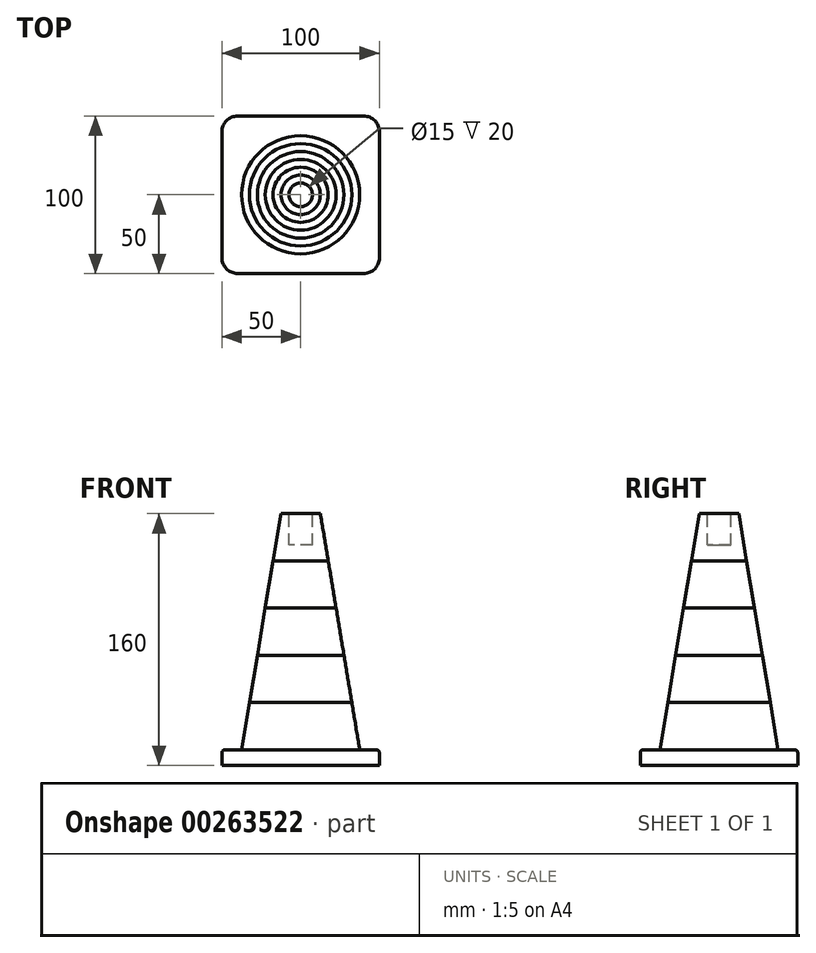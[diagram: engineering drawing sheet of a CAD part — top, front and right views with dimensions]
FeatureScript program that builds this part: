
annotation { "Feature Type Name" : "Feature", "Feature Type Description" : "" }
export const myFeature = defineFeature(function(context is Context, id is Id, definition is map)
    precondition{}
    {
        {
            var Q0;
            Q0=qCreatedBy(makeId("Top.planeOp"),FACE);
            var sketch = newSketch(context, id + "F0", { "sketchPlane" : qUnion([Q0])});
            skLineSegment(sketch, "E0.bottom", {"start": v(-40, 50) * mm, "end": v(40, 50) * mm});
            skLineSegment(sketch, "E0.top", {"start": v(-40, -50) * mm, "end": v(40, -50) * mm});
            skLineSegment(sketch, "E0.left", {"start": v(-50, 40) * mm, "end": v(-50, -40) * mm});
            skLineSegment(sketch, "E0.right", {"start": v(50, 40) * mm, "end": v(50, -40) * mm});
            skPoint(sketch, "E1.visualSharp", {"position": v(-50, 50) * mm});
            skArc(sketch, "E1.filletArc", {"start": v(-40, 50) * mm, "mid": v(-47.07, 47.07) * mm, "end": v(-50, 40) * mm});
            skPoint(sketch, "E2.visualSharp", {"position": v(50, 50) * mm});
            skArc(sketch, "E2.filletArc", {"start": v(50, 40) * mm, "mid": v(47.07, 47.07) * mm, "end": v(40, 50) * mm});
            skPoint(sketch, "E3.visualSharp", {"position": v(50, -50) * mm});
            skArc(sketch, "E3.filletArc", {"start": v(40, -50) * mm, "mid": v(47.07, -47.07) * mm, "end": v(50, -40) * mm});
            skPoint(sketch, "E4.visualSharp", {"position": v(-50, -50) * mm});
            skArc(sketch, "E4.filletArc", {"start": v(-50, -40) * mm, "mid": v(-47.07, -47.07) * mm, "end": v(-40, -50) * mm});
            skSolve(sketch);
        }
        {
            var Q0;
            Q0=makeQuery(id+"F0.imprint","IMPRINT",FACE,{"disambiguationData":[TD([[makeQuery(id+"F0.imprint","IMPRINT",EDGE,{"derivedFrom":sQuery(id+"F0.wireOp",EDGE,"E0.bottom")}),-1.0]])]});
            extrude(context, id + "F1", {"entities" : qUnion([Q0]), "depth" : 10 * mm});
        }
        {
            var Q0;
            Q0=makeQuery(id+"F1.opExtrude","CAP_FACE",FACE,{"disambiguationData":[OSD([sQuery(id+"F0.wireOp",EDGE,"E0.bottom"),sQuery(id+"F0.wireOp",EDGE,"E0.top"),sQuery(id+"F0.wireOp",EDGE,"E0.left"),sQuery(id+"F0.wireOp",EDGE,"E0.right")])],"isStart":false});
            var sketch = newSketch(context, id + "F2", { "sketchPlane" : qUnion([Q0])});
            skLineSegment(sketch, "E5.0.0", {"start": v(-50, 40) * mm, "end": v(-50, -40) * mm});
            skLineSegment(sketch, "E5.0.1", {"start": v(-50, -50) * mm, "end": v(-40, -50) * mm});
            skLineSegment(sketch, "E5.0.2", {"start": v(50, -50) * mm, "end": v(50, 40) * mm});
            skLineSegment(sketch, "E5.0.3", {"start": v(50, 50) * mm, "end": v(-50, 50) * mm});
            skCircle(sketch, "E6", {"center": v(0, 0) * mm, "radius": 37.5 * mm});
            skSolve(sketch);
        }
        {
            var Q0;
            Q0=qCreatedBy(makeId("Top.planeOp"),FACE);
            cPlane(context, id + "F3", {"entities" : qUnion([Q0]), "cplaneType" : CPlaneType.OFFSET, "offset" : 40 * mm, "width" : 150 * mm, "height" : 150 * mm});
        }
        {
            var Q0;
            Q0=qCreatedBy(id+"F3.planeOp",FACE);
            var sketch = newSketch(context, id + "F4", { "sketchPlane" : qUnion([Q0])});
            skCircle(sketch, "E7.0", {"center": v(0, 0) * mm, "radius": 37.5 * mm});
            skCircle(sketch, "E8", {"center": v(0, 0) * mm, "radius": 32.5 * mm});
            skSolve(sketch);
        }
        {
            var Q1;
            Q1=makeQuery(id+"F2.imprint","IMPRINT",FACE,{"disambiguationData":[TD([[makeQuery(id+"F2.imprint","IMPRINT",EDGE,{"derivedFrom":sQuery(id+"F2.wireOp",EDGE,"E6")}),1.0]])]});
            var Q2;
            Q2=makeQuery(id+"F4.imprint","IMPRINT",FACE,{"disambiguationData":[TD([[makeQuery(id+"F4.imprint","IMPRINT",EDGE,{"derivedFrom":sQuery(id+"F4.wireOp",EDGE,"E8")}),1.0]])]});
            loft(context, id + "F5", {"sheetProfilesArray" : [{ "sheetProfileEntities" : qUnion([Q1]) }, { "sheetProfileEntities" : qUnion([Q2]) }]});
        }
        {
            var Q0;
            Q0=qCreatedBy(id+"F3.planeOp",FACE);
            cPlane(context, id + "F6", {"entities" : qUnion([Q0]), "cplaneType" : CPlaneType.OFFSET, "offset" : 30 * mm, "width" : 150 * mm, "height" : 150 * mm});
        }
        {
            var Q0;
            Q0=qCreatedBy(id+"F6.planeOp",FACE);
            var sketch = newSketch(context, id + "F7", { "sketchPlane" : qUnion([Q0])});
            skCircle(sketch, "E9.0.0", {"center": v(0, 0) * mm, "radius": 32.5 * mm});
            skCircle(sketch, "E10", {"center": v(0, 0) * mm, "radius": 27.5 * mm});
            skSolve(sketch);
        }
        {
            var Q1;
            Q1=makeQuery(id+"F5.opLoft","CAP_FACE",FACE,{"disambiguationData":[OSD([makeQuery(id+"F4.imprint","IMPRINT",FACE,{"disambiguationData":[TD([[makeQuery(id+"F4.imprint","IMPRINT",EDGE,{"derivedFrom":sQuery(id+"F4.wireOp",EDGE,"E8")}),1.0]])]})])],"isStart":true});
            var Q2;
            Q2=makeQuery(id+"F7.imprint","IMPRINT",FACE,{"disambiguationData":[TD([[makeQuery(id+"F7.imprint","IMPRINT",EDGE,{"derivedFrom":sQuery(id+"F7.wireOp",EDGE,"E10")}),1.0]])]});
            loft(context, id + "F8", {"sheetProfilesArray" : [{ "sheetProfileEntities" : qUnion([Q1]) }, { "sheetProfileEntities" : qUnion([Q2]) }]});
        }
        {
            var Q0;
            Q0=qCreatedBy(id+"F6.planeOp",FACE);
            cPlane(context, id + "F9", {"entities" : qUnion([Q0]), "cplaneType" : CPlaneType.OFFSET, "offset" : 30 * mm, "width" : 150 * mm, "height" : 150 * mm});
        }
        {
            var Q0;
            Q0=qCreatedBy(id+"F9.planeOp",FACE);
            var sketch = newSketch(context, id + "F10", { "sketchPlane" : qUnion([Q0])});
            skCircle(sketch, "E11.0.0", {"center": v(0, 0) * mm, "radius": 27.5 * mm});
            skCircle(sketch, "E12", {"center": v(0, 0) * mm, "radius": 22.5 * mm});
            skSolve(sketch);
        }
        {
            var Q1;
            Q1=makeQuery(id+"F8.opLoft","CAP_FACE",FACE,{"disambiguationData":[OSD([makeQuery(id+"F7.imprint","IMPRINT",FACE,{"disambiguationData":[TD([[makeQuery(id+"F7.imprint","IMPRINT",EDGE,{"derivedFrom":sQuery(id+"F7.wireOp",EDGE,"E10")}),1.0]])]})])],"isStart":true});
            var Q2;
            Q2=makeQuery(id+"F10.imprint","IMPRINT",FACE,{"disambiguationData":[TD([[makeQuery(id+"F10.imprint","IMPRINT",EDGE,{"derivedFrom":sQuery(id+"F10.wireOp",EDGE,"E12")}),1.0]])]});
            loft(context, id + "F11", {"sheetProfilesArray" : [{ "sheetProfileEntities" : qUnion([Q1]) }, { "sheetProfileEntities" : qUnion([Q2]) }]});
        }
        {
            var Q0;
            Q0=qCreatedBy(id+"F9.planeOp",FACE);
            cPlane(context, id + "F12", {"entities" : qUnion([Q0]), "cplaneType" : CPlaneType.OFFSET, "offset" : 30 * mm, "width" : 150 * mm, "height" : 150 * mm});
        }
        {
            var Q0;
            Q0=qCreatedBy(id+"F12.planeOp",FACE);
            var sketch = newSketch(context, id + "F13", { "sketchPlane" : qUnion([Q0])});
            skCircle(sketch, "E13.0.0", {"center": v(0, 0) * mm, "radius": 22.5 * mm});
            skCircle(sketch, "E14", {"center": v(0, 0) * mm, "radius": 17.5 * mm});
            skSolve(sketch);
        }
        {
            var Q1;
            Q1=makeQuery(id+"F11.opLoft","CAP_FACE",FACE,{"disambiguationData":[OSD([makeQuery(id+"F10.imprint","IMPRINT",FACE,{"disambiguationData":[TD([[makeQuery(id+"F10.imprint","IMPRINT",EDGE,{"derivedFrom":sQuery(id+"F10.wireOp",EDGE,"E12")}),1.0]])]})])],"isStart":true});
            var Q2;
            Q2=makeQuery(id+"F13.imprint","IMPRINT",FACE,{"disambiguationData":[TD([[makeQuery(id+"F13.imprint","IMPRINT",EDGE,{"derivedFrom":sQuery(id+"F13.wireOp",EDGE,"E14")}),1.0]])]});
            loft(context, id + "F14", {"sheetProfilesArray" : [{ "sheetProfileEntities" : qUnion([Q1]) }, { "sheetProfileEntities" : qUnion([Q2]) }]});
        }
        {
            var Q0;
            Q0=qCreatedBy(id+"F12.planeOp",FACE);
            cPlane(context, id + "F15", {"entities" : qUnion([Q0]), "cplaneType" : CPlaneType.OFFSET, "offset" : 30 * mm, "width" : 150 * mm, "height" : 150 * mm});
        }
        {
            var Q0;
            Q0=qCreatedBy(id+"F15.planeOp",FACE);
            var sketch = newSketch(context, id + "F16", { "sketchPlane" : qUnion([Q0])});
            skCircle(sketch, "E15.0.0", {"center": v(0, 0) * mm, "radius": 17.5 * mm});
            skCircle(sketch, "E16", {"center": v(0, 0) * mm, "radius": 12.5 * mm});
            skSolve(sketch);
        }
        {
            var Q1;
            Q1=makeQuery(id+"F14.opLoft","CAP_FACE",FACE,{"disambiguationData":[OSD([makeQuery(id+"F13.imprint","IMPRINT",FACE,{"disambiguationData":[TD([[makeQuery(id+"F13.imprint","IMPRINT",EDGE,{"derivedFrom":sQuery(id+"F13.wireOp",EDGE,"E14")}),1.0]])]})])],"isStart":true});
            var Q2;
            Q2=makeQuery(id+"F16.imprint","IMPRINT",FACE,{"disambiguationData":[TD([[makeQuery(id+"F16.imprint","IMPRINT",EDGE,{"derivedFrom":sQuery(id+"F16.wireOp",EDGE,"E16")}),1.0]])]});
            loft(context, id + "F17", {"sheetProfilesArray" : [{ "sheetProfileEntities" : qUnion([Q1]) }, { "sheetProfileEntities" : qUnion([Q2]) }]});
        }
        {
            var Q0;
            Q0=makeQuery(id+"F1.opExtrude","CAP_EDGE",EDGE,{"disambiguationData":[OSD([sQuery(id+"F0.wireOp",EDGE,"E0.top")])],"isStart":false});
            var Q1;
            Q1=makeQuery(id+"F1.opExtrude","CAP_EDGE",EDGE,{"disambiguationData":[OSD([sQuery(id+"F0.wireOp",EDGE,"E4.filletArc")])],"isStart":false});
            var Q2;
            Q2=makeQuery(id+"F1.opExtrude","CAP_EDGE",EDGE,{"disambiguationData":[OSD([sQuery(id+"F0.wireOp",EDGE,"E0.left")])],"isStart":false});
            var Q3;
            Q3=makeQuery(id+"F1.opExtrude","CAP_EDGE",EDGE,{"disambiguationData":[OSD([sQuery(id+"F0.wireOp",EDGE,"E3.filletArc")])],"isStart":false});
            var Q4;
            Q4=makeQuery(id+"F1.opExtrude","CAP_EDGE",EDGE,{"disambiguationData":[OSD([sQuery(id+"F0.wireOp",EDGE,"E0.right")])],"isStart":false});
            var Q5;
            Q5=makeQuery(id+"F1.opExtrude","CAP_EDGE",EDGE,{"disambiguationData":[OSD([sQuery(id+"F0.wireOp",EDGE,"E2.filletArc")])],"isStart":false});
            var Q6;
            Q6=makeQuery(id+"F1.opExtrude","CAP_EDGE",EDGE,{"disambiguationData":[OSD([sQuery(id+"F0.wireOp",EDGE,"E0.bottom")])],"isStart":false});
            var Q7;
            Q7=makeQuery(id+"F1.opExtrude","CAP_EDGE",EDGE,{"disambiguationData":[OSD([sQuery(id+"F0.wireOp",EDGE,"E1.filletArc")])],"isStart":false});
            fillet(context, id + "F18", {"entities" : qUnion([Q0, Q1, Q2, Q3, Q4, Q5, Q6, Q7]), "radius" : 2 * mm, "tangentPropagation" : true, "allowEdgeOverflow" : false});
        }
        {
            var Q0;
            Q0=makeQuery(id+"F17.opLoft","CAP_FACE",FACE,{"disambiguationData":[OSD([makeQuery(id+"F16.imprint","IMPRINT",FACE,{"disambiguationData":[TD([[makeQuery(id+"F16.imprint","IMPRINT",EDGE,{"derivedFrom":sQuery(id+"F16.wireOp",EDGE,"E16")}),1.0]])]})])],"isStart":true});
            var sketch = newSketch(context, id + "F19", { "sketchPlane" : qUnion([Q0])});
            skCircle(sketch, "E17.0.0", {"center": v(0, 0) * mm, "radius": 12.5 * mm});
            skCircle(sketch, "E18", {"center": v(0, 0) * mm, "radius": 7.5 * mm});
            skSolve(sketch);
        }
        {
            var Q0;
            Q0=makeQuery(id+"F19.imprint","IMPRINT",FACE,{"disambiguationData":[TD([[makeQuery(id+"F19.imprint","IMPRINT",EDGE,{"derivedFrom":sQuery(id+"F19.wireOp",EDGE,"E18")}),1.0]])]});
            extrude(context, id + "F20", {"entities" : qUnion([Q0]), "operationType" : NewBodyOperationType.REMOVE, "oppositeDirection" : true, "depth" : 20 * mm});
        }
    });
